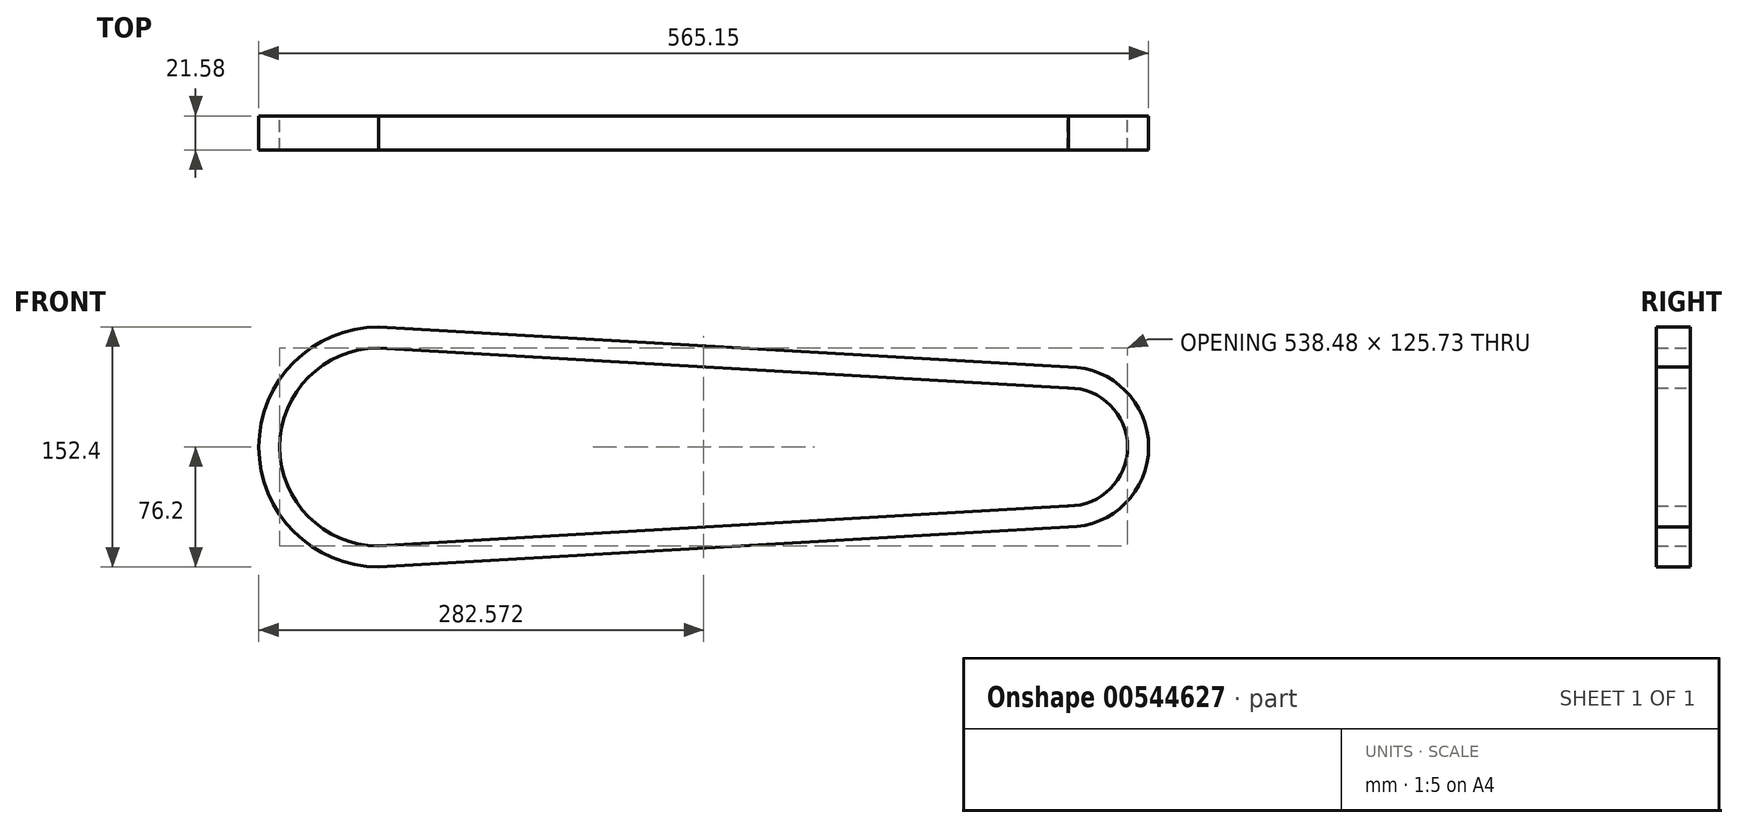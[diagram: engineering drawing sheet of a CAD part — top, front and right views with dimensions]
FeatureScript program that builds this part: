
annotation { "Feature Type Name" : "Feature", "Feature Type Description" : "" }
export const myFeature = defineFeature(function(context is Context, id is Id, definition is map)
    precondition{}
    {
        {
            var Q0;
            Q0=qCreatedBy(makeId("Front.planeOp"),FACE);
            var sketch = newSketch(context, id + "F0", { "sketchPlane" : qUnion([Q0])});
            skCircle(sketch, "E0", {"center": v(-127.2, 0) * mm, "radius": 76.2 * mm, "construction": true});
            skCircle(sketch, "E1", {"center": v(310.95, 0) * mm, "radius": 50.8 * mm, "construction": true});
            skArc(sketch, "E2", {"start": v(-127.2, 76.2) * mm, "mid": v(-203.4, 0) * mm, "end": v(-127.2, -76.2) * mm});
            skArc(sketch, "E3", {"start": v(310.95, -50.8) * mm, "mid": v(361.75, 0) * mm, "end": v(310.95, 50.8) * mm});
            skLineSegment(sketch, "E4", {"start": v(-127.2, 76.2) * mm, "end": v(310.95, 50.8) * mm});
            skLineSegment(sketch, "E5", {"start": v(-127.2, -76.2) * mm, "end": v(310.95, -50.8) * mm});
            skLineSegment(sketch, "E6.0", {"start": v(-127.57, -62.86) * mm, "end": v(310.18, -37.49) * mm});
            skArc(sketch, "E7.0", {"start": v(310.95, -37.46) * mm, "mid": v(348.41, 0) * mm, "end": v(310.95, 37.47) * mm});
            skLineSegment(sketch, "E8.0", {"start": v(-127.57, 62.86) * mm, "end": v(310.18, 37.49) * mm});
            skArc(sketch, "E9.0", {"start": v(-127.57, 62.86) * mm, "mid": v(-190.07, 0) * mm, "end": v(-127.57, -62.86) * mm});
            skLineSegment(sketch, "E10", {"start": v(310.95, -37.46) * mm, "end": v(310.18, -37.49) * mm});
            skLineSegment(sketch, "E11", {"start": v(310.18, 37.49) * mm, "end": v(310.95, 37.47) * mm});
            skSolve(sketch);
        }
        {
            var Q0;
            Q0=makeQuery(id+"F0.imprint","IMPRINT",FACE,{"disambiguationData":[TD([[makeQuery(id+"F0.imprint","IMPRINT",EDGE,{"derivedFrom":sQuery(id+"F0.wireOp",EDGE,"E2")}),1.0]])]});
            extrude(context, id + "F1", {"entities" : qUnion([Q0]), "endBound" : BoundingType.SYMMETRIC, "depth" : 21.59 * mm, "offsetDistance" : 25.4 * mm});
        }
    });
